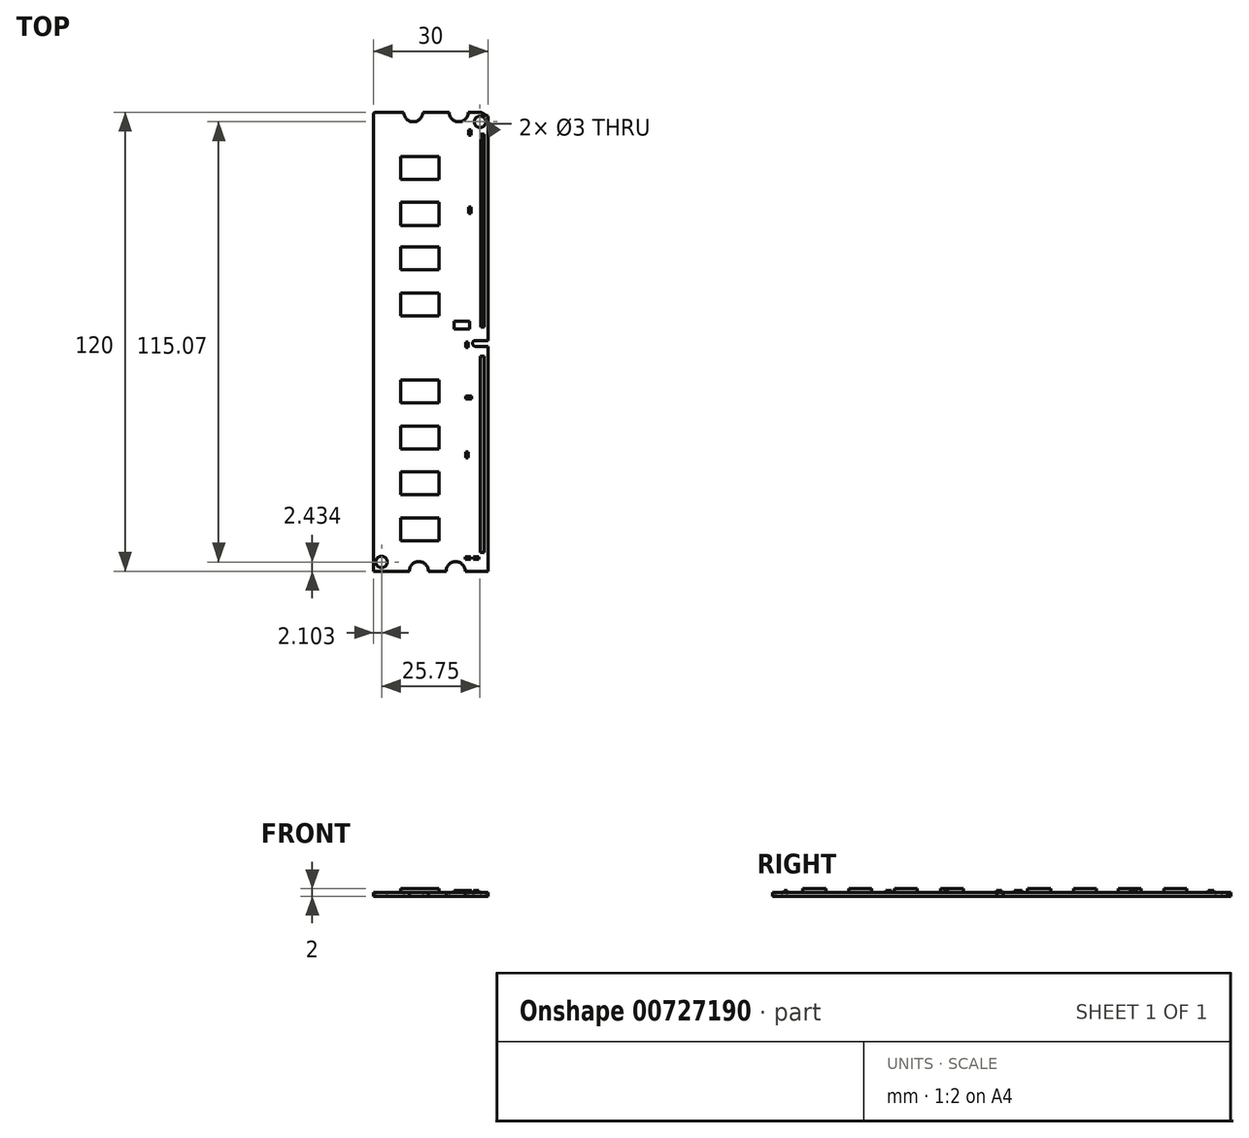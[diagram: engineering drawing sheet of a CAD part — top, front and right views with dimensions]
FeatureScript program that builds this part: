
annotation { "Feature Type Name" : "Feature", "Feature Type Description" : "" }
export const myFeature = defineFeature(function(context is Context, id is Id, definition is map)
    precondition{}
    {
        {
            var Q0;
            Q0=qCreatedBy(makeId("Top.planeOp"),FACE);
            var sketch = newSketch(context, id + "F0", { "sketchPlane" : qUnion([Q0])});
            skLineSegment(sketch, "E0", {"start": v(-47.66, 60.74) * mm, "end": v(-47.66, -59.26) * mm});
            skLineSegment(sketch, "E1", {"start": v(-47.66, 60.74) * mm, "end": v(-39.76, 60.74) * mm});
            skArc(sketch, "E2", {"start": v(-39.76, 60.74) * mm, "mid": v(-37.26, 58.24) * mm, "end": v(-34.76, 60.74) * mm});
            skArc(sketch, "E3", {"start": v(-27.88, 60.74) * mm, "mid": v(-25.38, 58.24) * mm, "end": v(-22.88, 60.74) * mm});
            skLineSegment(sketch, "E4.trimOffspring", {"start": v(-34.76, 60.74) * mm, "end": v(-27.88, 60.74) * mm});
            skLineSegment(sketch, "E5", {"start": v(-17.66, 59.76) * mm, "end": v(-17.66, 1.08) * mm});
            skLineSegment(sketch, "E6", {"start": v(-17.66, -59.26) * mm, "end": v(-23.67, -59.26) * mm});
            skLineSegment(sketch, "E7", {"start": v(-22.88, 60.74) * mm, "end": v(-19.64, 60.74) * mm});
            skLineSegment(sketch, "E8", {"start": v(-19.64, 60.74) * mm, "end": v(-17.66, 59.76) * mm});
            skLineSegment(sketch, "E9", {"start": v(-17.66, 1.08) * mm, "end": v(-20.99, 1.08) * mm});
            skLineSegment(sketch, "E10", {"start": v(-17.66, -0.46) * mm, "end": v(-20.99, -0.46) * mm});
            skLineSegment(sketch, "E11.trimOffspring", {"start": v(-17.66, -0.46) * mm, "end": v(-17.66, -59.26) * mm});
            skArc(sketch, "E12", {"start": v(-20.99, 1.08) * mm, "mid": v(-21.75, 0.31) * mm, "end": v(-20.99, -0.46) * mm});
            skArc(sketch, "E13", {"start": v(-23.67, -59.26) * mm, "mid": v(-26.17, -56.76) * mm, "end": v(-28.67, -59.26) * mm});
            skArc(sketch, "E14", {"start": v(-33.31, -59.26) * mm, "mid": v(-35.81, -56.76) * mm, "end": v(-38.31, -59.26) * mm});
            skLineSegment(sketch, "E15.trimOffspring", {"start": v(-38.31, -59.26) * mm, "end": v(-47.66, -59.26) * mm});
            skLineSegment(sketch, "E16.trimOffspring", {"start": v(-28.67, -59.26) * mm, "end": v(-33.31, -59.26) * mm});
            skSolve(sketch);
        }
        {
            var Q0;
            Q0=makeQuery(id+"F0.imprint","IMPRINT",FACE,{"disambiguationData":[TD([[makeQuery(id+"F0.imprint","IMPRINT",EDGE,{"derivedFrom":sQuery(id+"F0.wireOp",EDGE,"E0")}),1.0]])]});
            extrude(context, id + "F1", {"entities" : qUnion([Q0]), "depth" : 1 * mm, "offsetDistance" : 25 * mm});
        }
        {
            var Q0;
            Q0=makeQuery(id+"F1.opExtrude","CAP_FACE",FACE,{"disambiguationData":[OSD([sQuery(id+"F0.wireOp",EDGE,"E0"),sQuery(id+"F0.wireOp",EDGE,"E1"),sQuery(id+"F0.wireOp",EDGE,"E2"),sQuery(id+"F0.wireOp",EDGE,"E3"),sQuery(id+"F0.wireOp",EDGE,"E4.trimOffspring"),sQuery(id+"F0.wireOp",EDGE,"E5"),sQuery(id+"F0.wireOp",EDGE,"E6"),sQuery(id+"F0.wireOp",EDGE,"E7"),sQuery(id+"F0.wireOp",EDGE,"E8"),sQuery(id+"F0.wireOp",EDGE,"E9"),sQuery(id+"F0.wireOp",EDGE,"E10"),sQuery(id+"F0.wireOp",EDGE,"E11.trimOffspring"),sQuery(id+"F0.wireOp",EDGE,"E12"),sQuery(id+"F0.wireOp",EDGE,"E13"),sQuery(id+"F0.wireOp",EDGE,"E14"),sQuery(id+"F0.wireOp",EDGE,"E15.trimOffspring"),sQuery(id+"F0.wireOp",EDGE,"E16.trimOffspring")])],"isStart":false});
            var sketch = newSketch(context, id + "F2", { "sketchPlane" : qUnion([Q0])});
            skLineSegment(sketch, "E17", {"start": v(-40.5, 49.17) * mm, "end": v(-30.5, 49.17) * mm});
            skLineSegment(sketch, "E18", {"start": v(-30.5, 49.17) * mm, "end": v(-30.5, 43.17) * mm});
            skLineSegment(sketch, "E19", {"start": v(-30.5, 43.17) * mm, "end": v(-40.5, 43.17) * mm});
            skLineSegment(sketch, "E20", {"start": v(-40.5, 43.17) * mm, "end": v(-40.5, 49.17) * mm});
            skLineSegment(sketch, "E21", {"start": v(-40.5, 37.17) * mm, "end": v(-30.5, 37.17) * mm});
            skLineSegment(sketch, "E22", {"start": v(-30.5, 37.17) * mm, "end": v(-30.5, 31.17) * mm});
            skLineSegment(sketch, "E23", {"start": v(-30.5, 31.17) * mm, "end": v(-40.5, 31.17) * mm});
            skLineSegment(sketch, "E24", {"start": v(-40.5, 31.17) * mm, "end": v(-40.5, 37.17) * mm});
            skLineSegment(sketch, "E25", {"start": v(-30.5, 25.52) * mm, "end": v(-40.5, 25.52) * mm});
            skLineSegment(sketch, "E26", {"start": v(-40.5, 25.52) * mm, "end": v(-40.5, 19.52) * mm});
            skLineSegment(sketch, "E27", {"start": v(-40.5, 19.52) * mm, "end": v(-30.5, 19.52) * mm});
            skLineSegment(sketch, "E28", {"start": v(-30.5, 19.52) * mm, "end": v(-30.5, 25.52) * mm});
            skLineSegment(sketch, "E29", {"start": v(-40.5, 13.52) * mm, "end": v(-30.5, 13.52) * mm});
            skLineSegment(sketch, "E30", {"start": v(-30.5, 13.52) * mm, "end": v(-30.5, 7.52) * mm});
            skLineSegment(sketch, "E31", {"start": v(-30.5, 7.52) * mm, "end": v(-40.5, 7.52) * mm});
            skLineSegment(sketch, "E32", {"start": v(-40.5, 7.52) * mm, "end": v(-40.5, 13.52) * mm});
            skSolve(sketch);
        }
        {
            var Q0;
            Q0=makeQuery(id+"F2.imprint","IMPRINT",FACE,{"disambiguationData":[TD([[makeQuery(id+"F2.imprint","IMPRINT",EDGE,{"derivedFrom":sQuery(id+"F2.wireOp",EDGE,"E29")}),-1.0]])]});
            var Q1;
            Q1=makeQuery(id+"F2.imprint","IMPRINT",FACE,{"disambiguationData":[TD([[makeQuery(id+"F2.imprint","IMPRINT",EDGE,{"derivedFrom":sQuery(id+"F2.wireOp",EDGE,"E25")}),1.0]])]});
            var Q2;
            Q2=makeQuery(id+"F2.imprint","IMPRINT",FACE,{"disambiguationData":[TD([[makeQuery(id+"F2.imprint","IMPRINT",EDGE,{"derivedFrom":sQuery(id+"F2.wireOp",EDGE,"E21")}),-1.0]])]});
            var Q3;
            Q3=makeQuery(id+"F2.imprint","IMPRINT",FACE,{"disambiguationData":[TD([[makeQuery(id+"F2.imprint","IMPRINT",EDGE,{"derivedFrom":sQuery(id+"F2.wireOp",EDGE,"E17")}),-1.0]])]});
            extrude(context, id + "F3", {"entities" : qUnion([Q0, Q1, Q2, Q3]), "depth" : 1 * mm, "offsetDistance" : 25 * mm});
        }
        {
            var Q0;
            Q0=makeQuery(id+"F1.opExtrude","CAP_FACE",FACE,{"disambiguationData":[OSD([sQuery(id+"F0.wireOp",EDGE,"E0"),sQuery(id+"F0.wireOp",EDGE,"E1"),sQuery(id+"F0.wireOp",EDGE,"E2"),sQuery(id+"F0.wireOp",EDGE,"E3"),sQuery(id+"F0.wireOp",EDGE,"E4.trimOffspring"),sQuery(id+"F0.wireOp",EDGE,"E5"),sQuery(id+"F0.wireOp",EDGE,"E6"),sQuery(id+"F0.wireOp",EDGE,"E7"),sQuery(id+"F0.wireOp",EDGE,"E8"),sQuery(id+"F0.wireOp",EDGE,"E9"),sQuery(id+"F0.wireOp",EDGE,"E10"),sQuery(id+"F0.wireOp",EDGE,"E11.trimOffspring"),sQuery(id+"F0.wireOp",EDGE,"E12"),sQuery(id+"F0.wireOp",EDGE,"E13"),sQuery(id+"F0.wireOp",EDGE,"E14"),sQuery(id+"F0.wireOp",EDGE,"E15.trimOffspring"),sQuery(id+"F0.wireOp",EDGE,"E16.trimOffspring")])],"isStart":false});
            var sketch = newSketch(context, id + "F4", { "sketchPlane" : qUnion([Q0])});
            skLineSegment(sketch, "E33", {"start": v(-47.37, 60.74) * mm, "end": v(-47.66, 60.46) * mm});
            skSolve(sketch);
        }
        {
            var Q0;
            {var subQ0=sQuery(id+"F4.wireOp",EDGE,"E33");Q0=makeQuery(id+"F4.imprint","IMPRINT",FACE,{"disambiguationData":[TD([[makeQuery(id+"F4.imprint","IMPRINT",EDGE,{"derivedFrom":subQ0}),-1.0]])]});}
            extrude(context, id + "F5", {"entities" : qUnion([Q0]), "operationType" : NewBodyOperationType.REMOVE, "oppositeDirection" : true, "depth" : 25 * mm, "offsetDistance" : 25 * mm});
        }
        {
            var Q0;
            Q0=makeQuery(id+"F1.opExtrude","CAP_FACE",FACE,{"disambiguationData":[OSD([sQuery(id+"F0.wireOp",EDGE,"E0"),sQuery(id+"F0.wireOp",EDGE,"E1"),sQuery(id+"F0.wireOp",EDGE,"E2"),sQuery(id+"F0.wireOp",EDGE,"E3"),sQuery(id+"F0.wireOp",EDGE,"E4.trimOffspring"),sQuery(id+"F0.wireOp",EDGE,"E5"),sQuery(id+"F0.wireOp",EDGE,"E6"),sQuery(id+"F0.wireOp",EDGE,"E7"),sQuery(id+"F0.wireOp",EDGE,"E8"),sQuery(id+"F0.wireOp",EDGE,"E9"),sQuery(id+"F0.wireOp",EDGE,"E10"),sQuery(id+"F0.wireOp",EDGE,"E11.trimOffspring"),sQuery(id+"F0.wireOp",EDGE,"E12"),sQuery(id+"F0.wireOp",EDGE,"E13"),sQuery(id+"F0.wireOp",EDGE,"E14"),sQuery(id+"F0.wireOp",EDGE,"E15.trimOffspring"),sQuery(id+"F0.wireOp",EDGE,"E16.trimOffspring")])],"isStart":false});
            var sketch = newSketch(context, id + "F6", { "sketchPlane" : qUnion([Q0])});
            skCircle(sketch, "E34", {"center": v(-19.8, 58.24) * mm, "radius": 1.5 * mm});
            skPoint(sketch, "E34.centerSnap0", {"position": v(-25.38, 58.24) * mm});
            skCircle(sketch, "E35", {"center": v(-45.56, -56.83) * mm, "radius": 1.5 * mm});
            skSolve(sketch);
        }
        {
            var Q0;
            Q0=makeQuery(id+"F6.imprint","IMPRINT",FACE,{"disambiguationData":[TD([[makeQuery(id+"F6.imprint","IMPRINT",EDGE,{"derivedFrom":sQuery(id+"F6.wireOp",EDGE,"E34")}),1.0]])]});
            var Q1;
            Q1=makeQuery(id+"F6.imprint","IMPRINT",FACE,{"disambiguationData":[TD([[makeQuery(id+"F6.imprint","IMPRINT",EDGE,{"derivedFrom":sQuery(id+"F6.wireOp",EDGE,"E35")}),1.0]])]});
            extrude(context, id + "F7", {"entities" : qUnion([Q0, Q1]), "operationType" : NewBodyOperationType.REMOVE, "oppositeDirection" : true, "depth" : 25 * mm, "offsetDistance" : 25 * mm});
        }
        {
            var Q0;
            Q0=makeQuery(id+"F1.opExtrude","CAP_FACE",FACE,{"disambiguationData":[OSD([sQuery(id+"F0.wireOp",EDGE,"E0"),sQuery(id+"F0.wireOp",EDGE,"E1"),sQuery(id+"F0.wireOp",EDGE,"E2"),sQuery(id+"F0.wireOp",EDGE,"E3"),sQuery(id+"F0.wireOp",EDGE,"E4.trimOffspring"),sQuery(id+"F0.wireOp",EDGE,"E5"),sQuery(id+"F0.wireOp",EDGE,"E6"),sQuery(id+"F0.wireOp",EDGE,"E7"),sQuery(id+"F0.wireOp",EDGE,"E8"),sQuery(id+"F0.wireOp",EDGE,"E9"),sQuery(id+"F0.wireOp",EDGE,"E10"),sQuery(id+"F0.wireOp",EDGE,"E11.trimOffspring"),sQuery(id+"F0.wireOp",EDGE,"E12"),sQuery(id+"F0.wireOp",EDGE,"E13"),sQuery(id+"F0.wireOp",EDGE,"E14"),sQuery(id+"F0.wireOp",EDGE,"E15.trimOffspring"),sQuery(id+"F0.wireOp",EDGE,"E16.trimOffspring")])],"isStart":false});
            var sketch = newSketch(context, id + "F8", { "sketchPlane" : qUnion([Q0])});
            skLineSegment(sketch, "E36", {"start": v(-22.53, 4.05) * mm, "end": v(-26.53, 4.05) * mm});
            skLineSegment(sketch, "E37", {"start": v(-26.53, 4.05) * mm, "end": v(-26.53, 6.05) * mm});
            skLineSegment(sketch, "E38", {"start": v(-26.53, 6.05) * mm, "end": v(-22.53, 6.05) * mm});
            skLineSegment(sketch, "E39", {"start": v(-22.53, 6.05) * mm, "end": v(-22.53, 4.05) * mm});
            skLineSegment(sketch, "E40", {"start": v(-22.92, 0) * mm, "end": v(-22.92, 0.7) * mm});
            skLineSegment(sketch, "E41", {"start": v(-22.92, 0.7) * mm, "end": v(-23.54, 0.7) * mm});
            skLineSegment(sketch, "E42", {"start": v(-22.92, 0) * mm, "end": v(-22.92, -0.7) * mm});
            skLineSegment(sketch, "E43", {"start": v(-23.54, 0.7) * mm, "end": v(-23.54, -0.7) * mm});
            skLineSegment(sketch, "E44", {"start": v(-23.54, -0.7) * mm, "end": v(-22.92, -0.7) * mm});
            skSolve(sketch);
        }
        {
            var Q0;
            Q0=makeQuery(id+"F8.imprint","IMPRINT",FACE,{"disambiguationData":[TD([[makeQuery(id+"F8.imprint","IMPRINT",EDGE,{"derivedFrom":sQuery(id+"F8.wireOp",EDGE,"E40")}),1.0]])]});
            var Q1;
            Q1=makeQuery(id+"F8.imprint","IMPRINT",FACE,{"disambiguationData":[TD([[makeQuery(id+"F8.imprint","IMPRINT",EDGE,{"derivedFrom":sQuery(id+"F8.wireOp",EDGE,"E36")}),-1.0]])]});
            extrude(context, id + "F9", {"entities" : qUnion([Q0, Q1]), "depth" : 0.5 * mm, "offsetDistance" : 25 * mm});
        }
        {
            var Q0;
            Q0=makeQuery(id+"F1.opExtrude","CAP_FACE",FACE,{"disambiguationData":[OSD([sQuery(id+"F0.wireOp",EDGE,"E0"),sQuery(id+"F0.wireOp",EDGE,"E1"),sQuery(id+"F0.wireOp",EDGE,"E2"),sQuery(id+"F0.wireOp",EDGE,"E3"),sQuery(id+"F0.wireOp",EDGE,"E4.trimOffspring"),sQuery(id+"F0.wireOp",EDGE,"E5"),sQuery(id+"F0.wireOp",EDGE,"E6"),sQuery(id+"F0.wireOp",EDGE,"E7"),sQuery(id+"F0.wireOp",EDGE,"E8"),sQuery(id+"F0.wireOp",EDGE,"E9"),sQuery(id+"F0.wireOp",EDGE,"E10"),sQuery(id+"F0.wireOp",EDGE,"E11.trimOffspring"),sQuery(id+"F0.wireOp",EDGE,"E12"),sQuery(id+"F0.wireOp",EDGE,"E13"),sQuery(id+"F0.wireOp",EDGE,"E14"),sQuery(id+"F0.wireOp",EDGE,"E15.trimOffspring"),sQuery(id+"F0.wireOp",EDGE,"E16.trimOffspring")])],"isStart":false});
            var sketch = newSketch(context, id + "F10", { "sketchPlane" : qUnion([Q0])});
            skLineSegment(sketch, "E45", {"start": v(-40.5, -21.28) * mm, "end": v(-40.5, -27.28) * mm});
            skLineSegment(sketch, "E46", {"start": v(-40.5, -51.28) * mm, "end": v(-40.5, -45.28) * mm});
            skLineSegment(sketch, "E47", {"start": v(-40.5, -45.28) * mm, "end": v(-30.5, -45.28) * mm});
            skLineSegment(sketch, "E48", {"start": v(-30.5, -45.28) * mm, "end": v(-30.5, -51.28) * mm});
            skLineSegment(sketch, "E49", {"start": v(-30.5, -51.28) * mm, "end": v(-40.5, -51.28) * mm});
            skLineSegment(sketch, "E50", {"start": v(-40.5, -39.28) * mm, "end": v(-30.5, -39.28) * mm});
            skLineSegment(sketch, "E51", {"start": v(-30.5, -39.28) * mm, "end": v(-30.5, -33.28) * mm});
            skLineSegment(sketch, "E52", {"start": v(-30.5, -33.28) * mm, "end": v(-40.5, -33.28) * mm});
            skLineSegment(sketch, "E53", {"start": v(-40.5, -27.28) * mm, "end": v(-30.5, -27.28) * mm});
            skLineSegment(sketch, "E54", {"start": v(-30.5, -27.28) * mm, "end": v(-30.5, -21.28) * mm});
            skLineSegment(sketch, "E55", {"start": v(-30.5, -21.28) * mm, "end": v(-40.5, -21.28) * mm});
            skLineSegment(sketch, "E56", {"start": v(-40.5, -15.28) * mm, "end": v(-30.5, -15.28) * mm});
            skLineSegment(sketch, "E57", {"start": v(-30.5, -15.28) * mm, "end": v(-30.5, -9.28) * mm});
            skLineSegment(sketch, "E58", {"start": v(-30.5, -9.28) * mm, "end": v(-40.5, -9.28) * mm});
            skLineSegment(sketch, "E59", {"start": v(-40.5, -15.28) * mm, "end": v(-40.5, -9.28) * mm});
            skLineSegment(sketch, "E60.trimOffspring", {"start": v(-40.5, -33.28) * mm, "end": v(-40.5, -39.28) * mm});
            skLineSegment(sketch, "E61.trimOffspring", {"start": v(-40.5, -45.28) * mm, "end": v(-40.5, -51.28) * mm});
            skSolve(sketch);
        }
        {
            var Q0;
            Q0=makeQuery(id+"F10.imprint","IMPRINT",FACE,{"disambiguationData":[TD([[makeQuery(id+"F10.imprint","IMPRINT",EDGE,{"derivedFrom":sQuery(id+"F10.wireOp",EDGE,"E47")}),-1.0]])]});
            var Q1;
            Q1=makeQuery(id+"F10.imprint","IMPRINT",FACE,{"disambiguationData":[TD([[makeQuery(id+"F10.imprint","IMPRINT",EDGE,{"derivedFrom":sQuery(id+"F10.wireOp",EDGE,"E50")}),1.0]])]});
            var Q2;
            Q2=makeQuery(id+"F10.imprint","IMPRINT",FACE,{"disambiguationData":[TD([[makeQuery(id+"F10.imprint","IMPRINT",EDGE,{"derivedFrom":sQuery(id+"F10.wireOp",EDGE,"E45")}),1.0]])]});
            var Q3;
            Q3=makeQuery(id+"F10.imprint","IMPRINT",FACE,{"disambiguationData":[TD([[makeQuery(id+"F10.imprint","IMPRINT",EDGE,{"derivedFrom":sQuery(id+"F10.wireOp",EDGE,"E56")}),1.0]])]});
            extrude(context, id + "F11", {"entities" : qUnion([Q0, Q1, Q2, Q3]), "depth" : 1 * mm, "offsetDistance" : 25 * mm});
        }
        {
            var Q0;
            Q0=makeQuery(id+"F1.opExtrude","CAP_FACE",FACE,{"disambiguationData":[OSD([sQuery(id+"F0.wireOp",EDGE,"E0"),sQuery(id+"F0.wireOp",EDGE,"E1"),sQuery(id+"F0.wireOp",EDGE,"E2"),sQuery(id+"F0.wireOp",EDGE,"E3"),sQuery(id+"F0.wireOp",EDGE,"E4.trimOffspring"),sQuery(id+"F0.wireOp",EDGE,"E5"),sQuery(id+"F0.wireOp",EDGE,"E6"),sQuery(id+"F0.wireOp",EDGE,"E7"),sQuery(id+"F0.wireOp",EDGE,"E8"),sQuery(id+"F0.wireOp",EDGE,"E9"),sQuery(id+"F0.wireOp",EDGE,"E10"),sQuery(id+"F0.wireOp",EDGE,"E11.trimOffspring"),sQuery(id+"F0.wireOp",EDGE,"E12"),sQuery(id+"F0.wireOp",EDGE,"E13"),sQuery(id+"F0.wireOp",EDGE,"E14"),sQuery(id+"F0.wireOp",EDGE,"E15.trimOffspring"),sQuery(id+"F0.wireOp",EDGE,"E16.trimOffspring")])],"isStart":false});
            var sketch = newSketch(context, id + "F12", { "sketchPlane" : qUnion([Q0])});
            skLineSegment(sketch, "E62", {"start": v(-23.54, -13.44) * mm, "end": v(-22.07, -13.44) * mm});
            skLineSegment(sketch, "E63", {"start": v(-22.07, -13.44) * mm, "end": v(-22.07, -14.16) * mm});
            skLineSegment(sketch, "E64", {"start": v(-22.07, -14.16) * mm, "end": v(-23.54, -14.16) * mm});
            skLineSegment(sketch, "E65", {"start": v(-23.54, -14.16) * mm, "end": v(-23.54, -13.44) * mm});
            skLineSegment(sketch, "E66", {"start": v(-22.13, 56.2) * mm, "end": v(-22.13, 54.74) * mm});
            skLineSegment(sketch, "E67", {"start": v(-22.13, 54.74) * mm, "end": v(-22.77, 54.74) * mm});
            skLineSegment(sketch, "E68", {"start": v(-22.77, 54.74) * mm, "end": v(-22.77, 56.2) * mm});
            skLineSegment(sketch, "E69", {"start": v(-22.77, 56.2) * mm, "end": v(-22.13, 56.2) * mm});
            skSolve(sketch);
        }
        {
            var Q0;
            Q0=makeQuery(id+"F12.imprint","IMPRINT",FACE,{"disambiguationData":[TD([[makeQuery(id+"F12.imprint","IMPRINT",EDGE,{"derivedFrom":sQuery(id+"F12.wireOp",EDGE,"E66")}),-1.0]])]});
            var Q1;
            Q1=makeQuery(id+"F12.imprint","IMPRINT",FACE,{"disambiguationData":[TD([[makeQuery(id+"F12.imprint","IMPRINT",EDGE,{"derivedFrom":sQuery(id+"F12.wireOp",EDGE,"E62")}),-1.0]])]});
            extrude(context, id + "F13", {"entities" : qUnion([Q0, Q1]), "operationType" : NewBodyOperationType.ADD, "depth" : 0.5 * mm, "offsetDistance" : 25 * mm});
        }
        {
            var Q0;
            Q0=makeQuery(id+"F1.opExtrude","CAP_FACE",FACE,{"disambiguationData":[OSD([sQuery(id+"F0.wireOp",EDGE,"E0"),sQuery(id+"F0.wireOp",EDGE,"E1"),sQuery(id+"F0.wireOp",EDGE,"E2"),sQuery(id+"F0.wireOp",EDGE,"E3"),sQuery(id+"F0.wireOp",EDGE,"E4.trimOffspring"),sQuery(id+"F0.wireOp",EDGE,"E5"),sQuery(id+"F0.wireOp",EDGE,"E6"),sQuery(id+"F0.wireOp",EDGE,"E7"),sQuery(id+"F0.wireOp",EDGE,"E8"),sQuery(id+"F0.wireOp",EDGE,"E9"),sQuery(id+"F0.wireOp",EDGE,"E10"),sQuery(id+"F0.wireOp",EDGE,"E11.trimOffspring"),sQuery(id+"F0.wireOp",EDGE,"E12"),sQuery(id+"F0.wireOp",EDGE,"E13"),sQuery(id+"F0.wireOp",EDGE,"E14"),sQuery(id+"F0.wireOp",EDGE,"E15.trimOffspring"),sQuery(id+"F0.wireOp",EDGE,"E16.trimOffspring")])],"isStart":false});
            var sketch = newSketch(context, id + "F14", { "sketchPlane" : qUnion([Q0])});
            skLineSegment(sketch, "E70", {"start": v(-22.77, 35.9) * mm, "end": v(-22.77, 34.36) * mm});
            skPoint(sketch, "E70.startSnap0", {"position": v(-22.77, 55.47) * mm});
            skLineSegment(sketch, "E71", {"start": v(-22.77, 34.36) * mm, "end": v(-22.13, 34.36) * mm});
            skLineSegment(sketch, "E72", {"start": v(-22.13, 34.36) * mm, "end": v(-22.13, 35.9) * mm});
            skLineSegment(sketch, "E73", {"start": v(-22.13, 35.9) * mm, "end": v(-22.77, 35.9) * mm});
            skLineSegment(sketch, "E74", {"start": v(-22.88, -28.1) * mm, "end": v(-22.88, -29.6) * mm});
            skLineSegment(sketch, "E75", {"start": v(-22.88, -29.6) * mm, "end": v(-23.56, -29.6) * mm});
            skLineSegment(sketch, "E76", {"start": v(-23.56, -29.6) * mm, "end": v(-23.56, -28.1) * mm});
            skLineSegment(sketch, "E77", {"start": v(-23.56, -28.1) * mm, "end": v(-22.88, -28.1) * mm});
            skSolve(sketch);
        }
        {
            var Q0;
            Q0=makeQuery(id+"F14.imprint","IMPRINT",FACE,{"disambiguationData":[TD([[makeQuery(id+"F14.imprint","IMPRINT",EDGE,{"derivedFrom":sQuery(id+"F14.wireOp",EDGE,"E70")}),1.0]])]});
            var Q1;
            Q1=makeQuery(id+"F14.imprint","IMPRINT",FACE,{"disambiguationData":[TD([[makeQuery(id+"F14.imprint","IMPRINT",EDGE,{"derivedFrom":sQuery(id+"F14.wireOp",EDGE,"E74")}),-1.0]])]});
            extrude(context, id + "F15", {"entities" : qUnion([Q0, Q1]), "depth" : 0.5 * mm, "offsetDistance" : 25 * mm});
        }
        {
            var Q0;
            Q0=makeQuery(id+"F1.opExtrude","CAP_FACE",FACE,{"disambiguationData":[OSD([sQuery(id+"F0.wireOp",EDGE,"E0"),sQuery(id+"F0.wireOp",EDGE,"E1"),sQuery(id+"F0.wireOp",EDGE,"E2"),sQuery(id+"F0.wireOp",EDGE,"E3"),sQuery(id+"F0.wireOp",EDGE,"E4.trimOffspring"),sQuery(id+"F0.wireOp",EDGE,"E5"),sQuery(id+"F0.wireOp",EDGE,"E6"),sQuery(id+"F0.wireOp",EDGE,"E7"),sQuery(id+"F0.wireOp",EDGE,"E8"),sQuery(id+"F0.wireOp",EDGE,"E9"),sQuery(id+"F0.wireOp",EDGE,"E10"),sQuery(id+"F0.wireOp",EDGE,"E11.trimOffspring"),sQuery(id+"F0.wireOp",EDGE,"E12"),sQuery(id+"F0.wireOp",EDGE,"E13"),sQuery(id+"F0.wireOp",EDGE,"E14"),sQuery(id+"F0.wireOp",EDGE,"E15.trimOffspring"),sQuery(id+"F0.wireOp",EDGE,"E16.trimOffspring")])],"isStart":false});
            var sketch = newSketch(context, id + "F16", { "sketchPlane" : qUnion([Q0])});
            skLineSegment(sketch, "E78", {"start": v(-21.45, -55.43) * mm, "end": v(-20.11, -55.43) * mm});
            skLineSegment(sketch, "E79", {"start": v(-20.11, -55.43) * mm, "end": v(-20.11, -56.11) * mm});
            skLineSegment(sketch, "E80", {"start": v(-20.11, -56.11) * mm, "end": v(-21.45, -56.11) * mm});
            skLineSegment(sketch, "E81", {"start": v(-21.45, -56.11) * mm, "end": v(-21.45, -55.43) * mm});
            skLineSegment(sketch, "E82", {"start": v(-22.2, -56.11) * mm, "end": v(-23.69, -56.11) * mm});
            skLineSegment(sketch, "E83", {"start": v(-23.69, -56.11) * mm, "end": v(-23.69, -55.43) * mm});
            skLineSegment(sketch, "E84", {"start": v(-23.69, -55.43) * mm, "end": v(-22.2, -55.43) * mm});
            skLineSegment(sketch, "E85", {"start": v(-22.2, -55.43) * mm, "end": v(-22.2, -56.11) * mm});
            skSolve(sketch);
        }
        {
            var Q0;
            Q0=makeQuery(id+"F16.imprint","IMPRINT",FACE,{"disambiguationData":[TD([[makeQuery(id+"F16.imprint","IMPRINT",EDGE,{"derivedFrom":sQuery(id+"F16.wireOp",EDGE,"E82")}),-1.0]])]});
            var Q1;
            Q1=makeQuery(id+"F16.imprint","IMPRINT",FACE,{"disambiguationData":[TD([[makeQuery(id+"F16.imprint","IMPRINT",EDGE,{"derivedFrom":sQuery(id+"F16.wireOp",EDGE,"E78")}),-1.0]])]});
            extrude(context, id + "F17", {"entities" : qUnion([Q0, Q1]), "depth" : 0.5 * mm, "offsetDistance" : 25 * mm});
        }
        {
            var Q0;
            Q0=makeQuery(id+"F1.opExtrude","CAP_FACE",FACE,{"disambiguationData":[OSD([sQuery(id+"F0.wireOp",EDGE,"E0"),sQuery(id+"F0.wireOp",EDGE,"E1"),sQuery(id+"F0.wireOp",EDGE,"E2"),sQuery(id+"F0.wireOp",EDGE,"E3"),sQuery(id+"F0.wireOp",EDGE,"E4.trimOffspring"),sQuery(id+"F0.wireOp",EDGE,"E5"),sQuery(id+"F0.wireOp",EDGE,"E6"),sQuery(id+"F0.wireOp",EDGE,"E7"),sQuery(id+"F0.wireOp",EDGE,"E8"),sQuery(id+"F0.wireOp",EDGE,"E9"),sQuery(id+"F0.wireOp",EDGE,"E10"),sQuery(id+"F0.wireOp",EDGE,"E11.trimOffspring"),sQuery(id+"F0.wireOp",EDGE,"E12"),sQuery(id+"F0.wireOp",EDGE,"E13"),sQuery(id+"F0.wireOp",EDGE,"E14"),sQuery(id+"F0.wireOp",EDGE,"E15.trimOffspring"),sQuery(id+"F0.wireOp",EDGE,"E16.trimOffspring")])],"isStart":false});
            var sketch = newSketch(context, id + "F18", { "sketchPlane" : qUnion([Q0])});
            skLineSegment(sketch, "E86.bottom", {"start": v(-19.64, 55.04) * mm, "end": v(-18.7, 55.04) * mm});
            skLineSegment(sketch, "E86.top", {"start": v(-19.64, 55.04) * mm, "end": v(-18.7, 55.04) * mm});
            skLineSegment(sketch, "E86.left", {"start": v(-19.64, 55.04) * mm, "end": v(-19.64, 55.04) * mm});
            skLineSegment(sketch, "E86.right", {"start": v(-18.7, 55.04) * mm, "end": v(-18.7, 55.04) * mm});
            skLineSegment(sketch, "E87.bottom", {"start": v(-18.7, 55.04) * mm, "end": v(-19.64, 55.04) * mm});
            skLineSegment(sketch, "E87.top", {"start": v(-18.7, 4.63) * mm, "end": v(-19.64, 4.63) * mm});
            skLineSegment(sketch, "E87.left", {"start": v(-18.7, 55.04) * mm, "end": v(-18.7, 4.63) * mm});
            skLineSegment(sketch, "E87.right", {"start": v(-19.64, 55.04) * mm, "end": v(-19.64, 4.63) * mm});
            skSolve(sketch);
        }
        {
            var Q0;
            Q0 = qSketchRegion(id + "F18", true);
            extrude(context, id + "F19", {"entities" : qUnion([Q0]), "depth" : 0.01 * mm, "offsetDistance" : 25 * mm});
        }
        {
            var Q0;
            Q0=makeQuery(id+"F1.opExtrude","CAP_FACE",FACE,{"disambiguationData":[OSD([sQuery(id+"F0.wireOp",EDGE,"E0"),sQuery(id+"F0.wireOp",EDGE,"E1"),sQuery(id+"F0.wireOp",EDGE,"E2"),sQuery(id+"F0.wireOp",EDGE,"E3"),sQuery(id+"F0.wireOp",EDGE,"E4.trimOffspring"),sQuery(id+"F0.wireOp",EDGE,"E5"),sQuery(id+"F0.wireOp",EDGE,"E6"),sQuery(id+"F0.wireOp",EDGE,"E7"),sQuery(id+"F0.wireOp",EDGE,"E8"),sQuery(id+"F0.wireOp",EDGE,"E9"),sQuery(id+"F0.wireOp",EDGE,"E10"),sQuery(id+"F0.wireOp",EDGE,"E11.trimOffspring"),sQuery(id+"F0.wireOp",EDGE,"E12"),sQuery(id+"F0.wireOp",EDGE,"E13"),sQuery(id+"F0.wireOp",EDGE,"E14"),sQuery(id+"F0.wireOp",EDGE,"E15.trimOffspring"),sQuery(id+"F0.wireOp",EDGE,"E16.trimOffspring")])],"isStart":false});
            var sketch = newSketch(context, id + "F20", { "sketchPlane" : qUnion([Q0])});
            skLineSegment(sketch, "E88.bottom", {"start": v(-19.68, -2.98) * mm, "end": v(-18.74, -2.98) * mm});
            skLineSegment(sketch, "E88.top", {"start": v(-19.68, -54.34) * mm, "end": v(-18.74, -54.34) * mm});
            skLineSegment(sketch, "E88.left", {"start": v(-19.68, -2.98) * mm, "end": v(-19.68, -54.34) * mm});
            skLineSegment(sketch, "E88.right", {"start": v(-18.74, -2.98) * mm, "end": v(-18.74, -54.34) * mm});
            skSolve(sketch);
        }
        {
            var Q0;
            Q0=makeQuery(id+"F20.imprint","IMPRINT",FACE,{"disambiguationData":[TD([[makeQuery(id+"F20.imprint","IMPRINT",EDGE,{"derivedFrom":sQuery(id+"F20.wireOp",EDGE,"E88.bottom")}),-1.0]])]});
            extrude(context, id + "F21", {"entities" : qUnion([Q0]), "depth" : 0.01 * mm, "offsetDistance" : 25 * mm});
        }
    });
